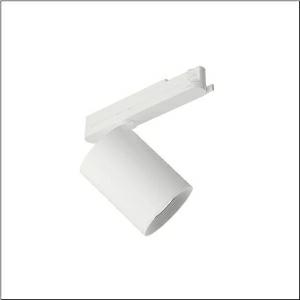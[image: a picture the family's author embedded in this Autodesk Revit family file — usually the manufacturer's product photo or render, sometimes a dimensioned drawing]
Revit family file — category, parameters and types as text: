
# Revit family: spot_11_51sd14mba5a
name_source: partatom
category: Lighting Fixtures
units: mm (PartAtom-declared; Revit-internal decimal feet)

## family parameters
Cut with Voids When Loaded = No
Host = Face
Light Source = No
Part Type = Normal
Room Calculation Point = No
Round Connector Dimension = Use Diameter
Shared = No

## types (1)
- --- (1 x LED, 7210 lm, 50.7 W, 2700K)
    Apparent Load = 51 VA
    CIE Flux Codes = 95 98 100 100 100
    Color Rendering = 90
    Color Temperature = 2700K
    Default Elevation = 1800 mm
    Description = Spot 11, directional spotlight, light control with lens, of PMMA, LED rated luminous flux: 5.550lm, light colour: 927, control gear: ECG Multilumen, with 3-phase adapter, mains connection: 220..240V, AC, 50/60Hz, of aluminium, traffic white (RAL 9016), length: 213mm, diameter: 105mm, protection rating (complete): IP20, insulation class (complete): insulation class I (protective earthing), certification: CE, impact resistance: IK02, permissible ambient temperature for indoor applications: -20..+40°C, packaging unit: 1 piece
    Height = 175 mm
    Lamp = 1 x LED
    Lamp Light Flux = 7210 lm
    Lamp Power = 50.7 W
    Lamp count = 1
    Length = 105 mm
    Luminous efficacy = 142 lm/W
    Manufacturer = Siteco
    ModVariant = No
    Model = 51SD14MBA5A
    Mounting Place = Ceiling
    Mounting Type = Pendant
    Number of Poles = 1
    OnlyDefault = Yes
    Power Factor = 1
    Product Name = Spot 11
    Product group = directional spotlight
    ProductGroupID = 905
    Protection Class = Protection class I
    Protection Degree = IP 20
    RLX_Detail_Level = 1
    RLX_Emergency_Light_Flux = 0 lm
    RLX_Emergency_Type = 0
    RLX_Emergency_Type_DB = No
    RlxData = <blob elided: 17689 chars, md5=fe2a82a1>
    Socket = socket
    Standby Power = 0 W
    System Light Flux = 7210 lm
    System Power = 51 W
    Type Comments = factory setting: luminous flux: 100 % | (ON | ON | ON | ON) | 1050 mA
    Type Image = l_1006697.jpg
    URL = http://relux.com
    VarID = @adj_168947
    Voltage = 0 V
    Weight = 0.00 kg
    Width = 0 mm  [stored 0 ft]

note: [stored X ft] marks values corroborated as IEEE doubles in the binary element streams (Revit-internal decimal feet)

## geometry (parser evidence)
native form markers: Blend x4, Sweep x9
no freeform markers — native parametric forms only
